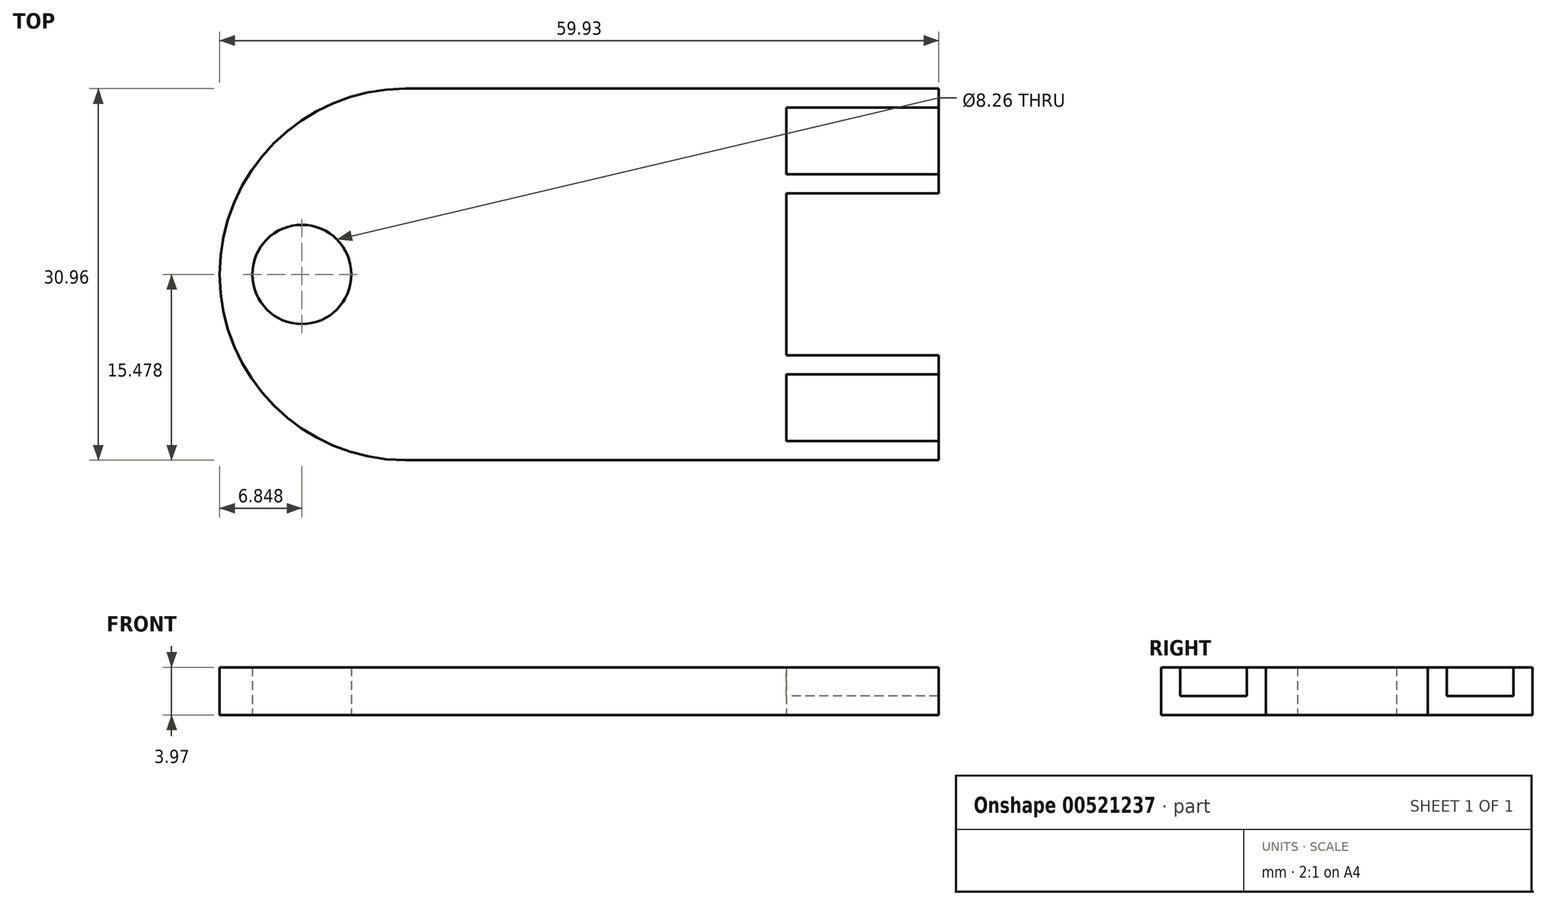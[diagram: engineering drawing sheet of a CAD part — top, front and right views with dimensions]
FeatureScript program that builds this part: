
annotation { "Feature Type Name" : "Feature", "Feature Type Description" : "" }
export const myFeature = defineFeature(function(context is Context, id is Id, definition is map)
    precondition{}
    {
        {
            var Q0;
            Q0=qCreatedBy(makeId("Top.planeOp"),FACE);
            var sketch = newSketch(context, id + "F0", { "sketchPlane" : qUnion([Q0])});
            skLineSegment(sketch, "E0", {"start": v(0, 0) * mm, "end": v(0, 30.96) * mm});
            skLineSegment(sketch, "E1", {"start": v(0, 30.96) * mm, "end": v(31.75, 30.96) * mm});
            skArc(sketch, "E2", {"start": v(0, 30.96) * mm, "mid": v(-15.48, 15.48) * mm, "end": v(0, 0) * mm});
            skLineSegment(sketch, "E3", {"start": v(0, 0) * mm, "end": v(31.75, 0) * mm});
            skLineSegment(sketch, "E4", {"start": v(31.75, 0) * mm, "end": v(31.75, 30.96) * mm});
            skLineSegment(sketch, "E5", {"start": v(31.75, 30.96) * mm, "end": v(44.45, 30.96) * mm});
            skLineSegment(sketch, "E6", {"start": v(44.45, 30.96) * mm, "end": v(44.45, 22.22) * mm});
            skLineSegment(sketch, "E7", {"start": v(44.45, 22.22) * mm, "end": v(31.75, 22.22) * mm});
            skLineSegment(sketch, "E8", {"start": v(31.75, 15.48) * mm, "end": v(-15.48, 15.48) * mm});
            skLineSegment(sketch, "E9.MirrorCS", {"start": v(44.45, 8.73) * mm, "end": v(31.75, 8.73) * mm});
            skLineSegment(sketch, "E10.MirrorCS", {"start": v(44.45, 0) * mm, "end": v(44.45, 8.73) * mm});
            skLineSegment(sketch, "E11.MirrorCS", {"start": v(31.75, 0) * mm, "end": v(44.45, 0) * mm});
            skCircle(sketch, "E12", {"center": v(-8.63, 15.48) * mm, "radius": 4.13 * mm});
            skSolve(sketch);
        }
        {
            var Q0;
            {var subQ1=sQuery(id+"F0.wireOp",EDGE,"E1");Q0=makeQuery(id+"F0.imprint","IMPRINT",FACE,{"disambiguationData":[TD([[makeQuery(id+"F0.imprint","IMPRINT",EDGE,{"derivedFrom":subQ1}),-1.0]])]});}
            var Q1;
            {var subQ0=sQuery(id+"F0.wireOp",EDGE,"E8");var subQ1=sQuery(id+"F0.wireOp",EDGE,"E0");var subQ2=makeQuery(id+"F0.imprint","INTERSECT",VERTEX,{"derivedFrom":[subQ1,subQ0]});Q1=makeQuery(id+"F0.imprint","IMPRINT",FACE,{"disambiguationData":[TD([[makeQuery(id+"F0.imprint","IMPRINT",EDGE,{"disambiguationData":[TD([[subQ2,-1.0]])],"derivedFrom":subQ0}),-1.0]])]});}
            var Q2;
            {var subQ0=sQuery(id+"F0.wireOp",EDGE,"E8");var subQ5=sQuery(id+"F0.wireOp",EDGE,"E0");var subQ6=makeQuery(id+"F0.imprint","INTERSECT",VERTEX,{"derivedFrom":[subQ5,subQ0]});Q2=makeQuery(id+"F0.imprint","IMPRINT",FACE,{"disambiguationData":[TD([[makeQuery(id+"F0.imprint","IMPRINT",EDGE,{"disambiguationData":[TD([[subQ6,-1.0]])],"derivedFrom":subQ0}),1.0]])]});}
            var Q3;
            {var subQ4=sQuery(id+"F0.wireOp",EDGE,"E3");Q3=makeQuery(id+"F0.imprint","IMPRINT",FACE,{"disambiguationData":[TD([[makeQuery(id+"F0.imprint","IMPRINT",EDGE,{"derivedFrom":subQ4}),1.0]])]});}
            var Q4;
            {var subQ2=sQuery(id+"F0.wireOp",EDGE,"E9.MirrorCS");Q4=makeQuery(id+"F0.imprint","IMPRINT",FACE,{"disambiguationData":[TD([[makeQuery(id+"F0.imprint","IMPRINT",EDGE,{"derivedFrom":subQ2}),1.0]])]});}
            var Q5;
            {var subQ0=sQuery(id+"F0.wireOp",EDGE,"E5");Q5=makeQuery(id+"F0.imprint","IMPRINT",FACE,{"disambiguationData":[TD([[makeQuery(id+"F0.imprint","IMPRINT",EDGE,{"derivedFrom":subQ0}),-1.0]])]});}
            extrude(context, id + "F1", {"entities" : qUnion([Q0, Q1, Q2, Q3, Q4, Q5]), "depth" : 3.97 * mm, "offsetDistance" : 25.4 * mm});
        }
        {
            var Q0;
            Q0=makeQuery(id+"F1.opExtrude","CAP_FACE",FACE,{"disambiguationData":[OSD([sQuery(id+"F0.wireOp",EDGE,"E1"),sQuery(id+"F0.wireOp",EDGE,"E2"),sQuery(id+"F0.wireOp",EDGE,"E3"),sQuery(id+"F0.wireOp",EDGE,"E4"),sQuery(id+"F0.wireOp",EDGE,"E5"),sQuery(id+"F0.wireOp",EDGE,"E6"),sQuery(id+"F0.wireOp",EDGE,"E7"),sQuery(id+"F0.wireOp",EDGE,"E9.MirrorCS"),sQuery(id+"F0.wireOp",EDGE,"E10.MirrorCS"),sQuery(id+"F0.wireOp",EDGE,"E11.MirrorCS"),sQuery(id+"F0.wireOp",EDGE,"E12")])],"isStart":false});
            var sketch = newSketch(context, id + "F2", { "sketchPlane" : qUnion([Q0])});
            skLineSegment(sketch, "E13", {"start": v(44.45, 29.37) * mm, "end": v(31.75, 29.37) * mm});
            skLineSegment(sketch, "E14", {"start": v(44.45, 29.37) * mm, "end": v(44.45, 30.96) * mm});
            skLineSegment(sketch, "E15", {"start": v(44.45, 30.96) * mm, "end": v(31.75, 30.96) * mm});
            skLineSegment(sketch, "E16", {"start": v(31.75, 30.96) * mm, "end": v(31.75, 29.37) * mm});
            skLineSegment(sketch, "E17", {"start": v(44.45, 26.6) * mm, "end": v(31.6, 26.6) * mm});
            skLineSegment(sketch, "E18.MirrorCS", {"start": v(44.45, 23.81) * mm, "end": v(31.75, 23.81) * mm});
            skLineSegment(sketch, "E19.MirrorCS", {"start": v(44.45, 23.81) * mm, "end": v(44.45, 22.22) * mm});
            skLineSegment(sketch, "E20.MirrorCS", {"start": v(44.45, 22.22) * mm, "end": v(31.75, 22.22) * mm});
            skLineSegment(sketch, "E21.MirrorCS", {"start": v(31.75, 22.22) * mm, "end": v(31.75, 23.81) * mm});
            skLineSegment(sketch, "E22", {"start": v(31.75, 15.48) * mm, "end": v(44.16, 15.48) * mm});
            skLineSegment(sketch, "E23.MirrorCS", {"start": v(44.45, 8.73) * mm, "end": v(31.75, 8.73) * mm});
            skLineSegment(sketch, "E24.MirrorCS", {"start": v(44.45, 7.14) * mm, "end": v(31.75, 7.14) * mm});
            skLineSegment(sketch, "E25.MirrorCS", {"start": v(31.75, 8.73) * mm, "end": v(31.75, 7.14) * mm});
            skLineSegment(sketch, "E26.MirrorCS", {"start": v(44.45, 7.14) * mm, "end": v(44.45, 8.73) * mm});
            skLineSegment(sketch, "E27.MirrorCS", {"start": v(44.45, 1.59) * mm, "end": v(31.75, 1.59) * mm});
            skLineSegment(sketch, "E28.MirrorCS", {"start": v(44.45, 1.59) * mm, "end": v(44.45, 0) * mm});
            skLineSegment(sketch, "E29.MirrorCS", {"start": v(44.45, 0) * mm, "end": v(31.75, 0) * mm});
            skLineSegment(sketch, "E30.MirrorCS", {"start": v(31.75, 0) * mm, "end": v(31.75, 1.59) * mm});
            skLineSegment(sketch, "E31", {"start": v(31.75, 29.37) * mm, "end": v(31.75, 23.81) * mm});
            skLineSegment(sketch, "E32", {"start": v(44.45, 29.37) * mm, "end": v(44.45, 23.81) * mm});
            skLineSegment(sketch, "E33", {"start": v(44.45, 7.14) * mm, "end": v(44.45, 1.59) * mm});
            skLineSegment(sketch, "E34", {"start": v(31.75, 7.14) * mm, "end": v(31.75, 1.59) * mm});
            skSolve(sketch);
        }
        {
            var Q0;
            {var subQ0=sQuery(id+"F2.wireOp",EDGE,"E13");Q0=makeQuery(id+"F2.imprint","IMPRINT",FACE,{"disambiguationData":[TD([[makeQuery(id+"F2.imprint","IMPRINT",EDGE,{"derivedFrom":subQ0}),1.0]])]});}
            var Q1;
            {var subQ5=sQuery(id+"F2.wireOp",EDGE,"E18.MirrorCS");Q1=makeQuery(id+"F2.imprint","IMPRINT",FACE,{"disambiguationData":[TD([[makeQuery(id+"F2.imprint","IMPRINT",EDGE,{"derivedFrom":subQ5}),-1.0]])]});}
            var Q2;
            Q2=makeQuery(id+"F2.imprint","IMPRINT",FACE,{"disambiguationData":[TD([[makeQuery(id+"F2.imprint","IMPRINT",EDGE,{"derivedFrom":sQuery(id+"F2.wireOp",EDGE,"E24.MirrorCS")}),1.0]])]});
            extrude(context, id + "F3", {"entities" : qUnion([Q0, Q1, Q2]), "operationType" : NewBodyOperationType.REMOVE, "oppositeDirection" : true, "depth" : 2.38 * mm, "offsetDistance" : 25.4 * mm});
        }
    });
